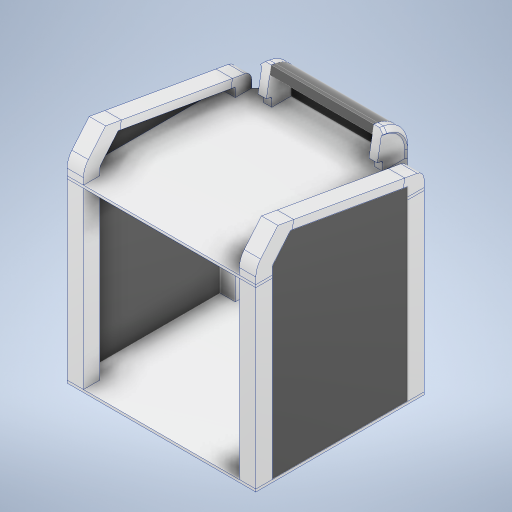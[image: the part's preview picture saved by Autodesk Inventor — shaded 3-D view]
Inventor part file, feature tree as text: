
AUTODESK INVENTOR PART (.ipt)
format: ipt  version: 2024 (Build 280153000, 153)  size: 794,112 bytes
history: native  units: mm
features: projected_geometry x24, extrude x16, sketch x15, other x9, mirror x5, fillet x4, revolve x2, plane x2
ambient origin geometry x8: Origin, YZ Plane, XZ Plane, XY Plane, X Axis, Y Axis, Z Axis, Center Point
bodies: Solid1 (feature_tree)
feature tree (77):
  sketch  "Sketch1"  dims[d0=460.0mm d1=410.0mm]
  extrude  "Extrusion1"  Depth=410.0mm
  revolve  "Revolution1"  [1 undecoded]
  sketch  "Sketch3"  dims[d4=135.0deg d5=135.0deg]
  plane  "Work Plane4"
  extrude  "Extrusion5"  TaperAngle=135.0deg  [1 undecoded]
  extrude  "Extrusion6"  Depth=20.0mm
  fillet  "Fillet1"  Radius=13.962634mm
  fillet  "Fillet3"  [1 undecoded]
  fillet  "Fillet4"  Radius=10.0mm
  fillet  "Fillet5"  Radius=10.0mm
  extrude  "Extrusion7"  Depth=2.0mm
  sketch  "Sketch8"  dims[d25=50.0mm d27=2.0mm]
  extrude  "Extrusion8"  Depth=2.0mm
  extrude  "Extrusion9"  Depth=10.0mm
  sketch  "Sketch10"  dims[d30=67.5deg d32=10.0mm]
  extrude  "Extrusion10"  Depth=40.0mm
  mirror  "Mirror1"
  extrude  "Extrusion11"  Depth=40.0mm
  mirror  "Mirror2"
  extrude  "Extrusion12"  Depth=250.0mm
  mirror  "Mirror3"
  extrude  "Extrusion13"  Depth=40.0mm
  mirror  "Mirror4"
  sketch  "Sketch14"  dims[d38=250.0mm d39=60.0mm]
  extrude  "Extrusion14"  Depth=40.0mm
  extrude  "Extrusion15"  Depth=40.0mm
  extrude  "Extrusion16"  Depth=40.0mm
  extrude  "Extrusion17"  Depth=10.0mm
  extrude  "Extrusion18"  Depth=3.175mm
  revolve  "Revolution2"  [1 undecoded]
  extrude  "Extrusion19"  Depth=40.0mm
  mirror  "Mirror5"
  sketch  "Sketch2"  dims[d2=40.0mm d3=40.0mm]
  projected_geometry  "Projected Loop1"
  projected_geometry  "Projected Loop2"
  plane  "Work Plane3"
  sketch  "Sketch6"  dims[d7=450.0mm d8=0.0mm d9=20.0mm d10=13.962634mm d20=-10.0mm d21=10.0mm d22=0.0mm d23=10.0mm d24=0.0mm]
  projected_geometry  "Projected Loop4"
  other  "Base Plate"
  projected_geometry  "Projected Loop5"
  other  "Verticals"
  sketch  "Sketch9"  dims[d28=2.0mm d29=2.0mm]
  projected_geometry  "Projected Loop6"
  other  "Gantry Plate"
  projected_geometry  "Projected Loop7"
  projected_geometry  "Projected Loop8"
  projected_geometry  "Projected Loop9"
  projected_geometry  "Projected Loop10"
  projected_geometry  "Projected Loop11"
  projected_geometry  "Projected Loop12"
  other  "Printed Top Bar Holders"
  other  "Top Bars"
  sketch  "Sketch12"  dims[d34=50.857864mm d35=40.0mm]
  projected_geometry  "Projected Loop13"
  projected_geometry  "Projected Loop14"
  projected_geometry  "Projected Loop15"
  sketch  "Sketch13"  dims[d36=40.0mm d37=300.0mm]
  other  "Side Shear Panels"
  other  "Rear Curve Panel"
  sketch  "Sketch15"  dims[d40=40.0mm d41=40.0mm]
  projected_geometry  "Projected Loop16"
  projected_geometry  "Projected Loop17"
  projected_geometry  "Projected Loop18"
  sketch  "Sketch16"  dims[d42=40.0mm d43=40.0mm]
  projected_geometry  "Projected Loop19"
  projected_geometry  "Projected Loop20"
  other  "Rear Shear Panel"
  sketch  "Sketch17"  dims[d44=40.0mm d45=40.0mm]
  projected_geometry  "Projected Loop21"
  projected_geometry  "Projected Loop22"
  other  "Rear Line Panel"
  sketch  "Sketch18"  dims[d46=80.0mm d47=40.0mm]
  projected_geometry  "Projected Loop23"
  sketch  "Sketch19"  dims[d48=10.0mm d50=10.0mm d51=3.0mm d52=26.0mm d53=40.0mm d54=20.0mm d55=55.0mm d56=105.0mm d57=90.0mm d58=220.0mm d59=8.0mm d60=20.0mm d61=55.0mm d62=150.0deg d63=6.35mm d64=0.0mm d65=55.0mm d66=425.0mm d67=0.0mm d68=6.35mm d69=0.0mm d70=20.0mm d71=40.0mm d72=20.0mm d73=2.0mm d74=40.0mm d76=2.0mm d77=275.0mm d78=40.0mm d79=0.0mm d80=40.0mm d81=0.0mm d82=3.5mm d83=0.0mm d84=0.5mm d85=3.175mm d86=0.0mm d88=10.0mm d89=20.0mm d90=3.175mm d91=0.0mm d92=10.0mm d93=0.0mm d94=3.5mm d95=0.0mm d96=0.5mm d97=3.175mm d98=0.0mm d99=5.0mm d100=18.65mm d101=0.0mm d102=13.962634mm d103=0.0mm d104=0.0mm]
  projected_geometry  "Projected Loop24"
  projected_geometry  "Project Cut Edges1"
note: 4 required parameter values undecoded (feature->parameter linkage not recoverable at this tier; creation-order binding heuristic only, values carry confidence <= 0.55)